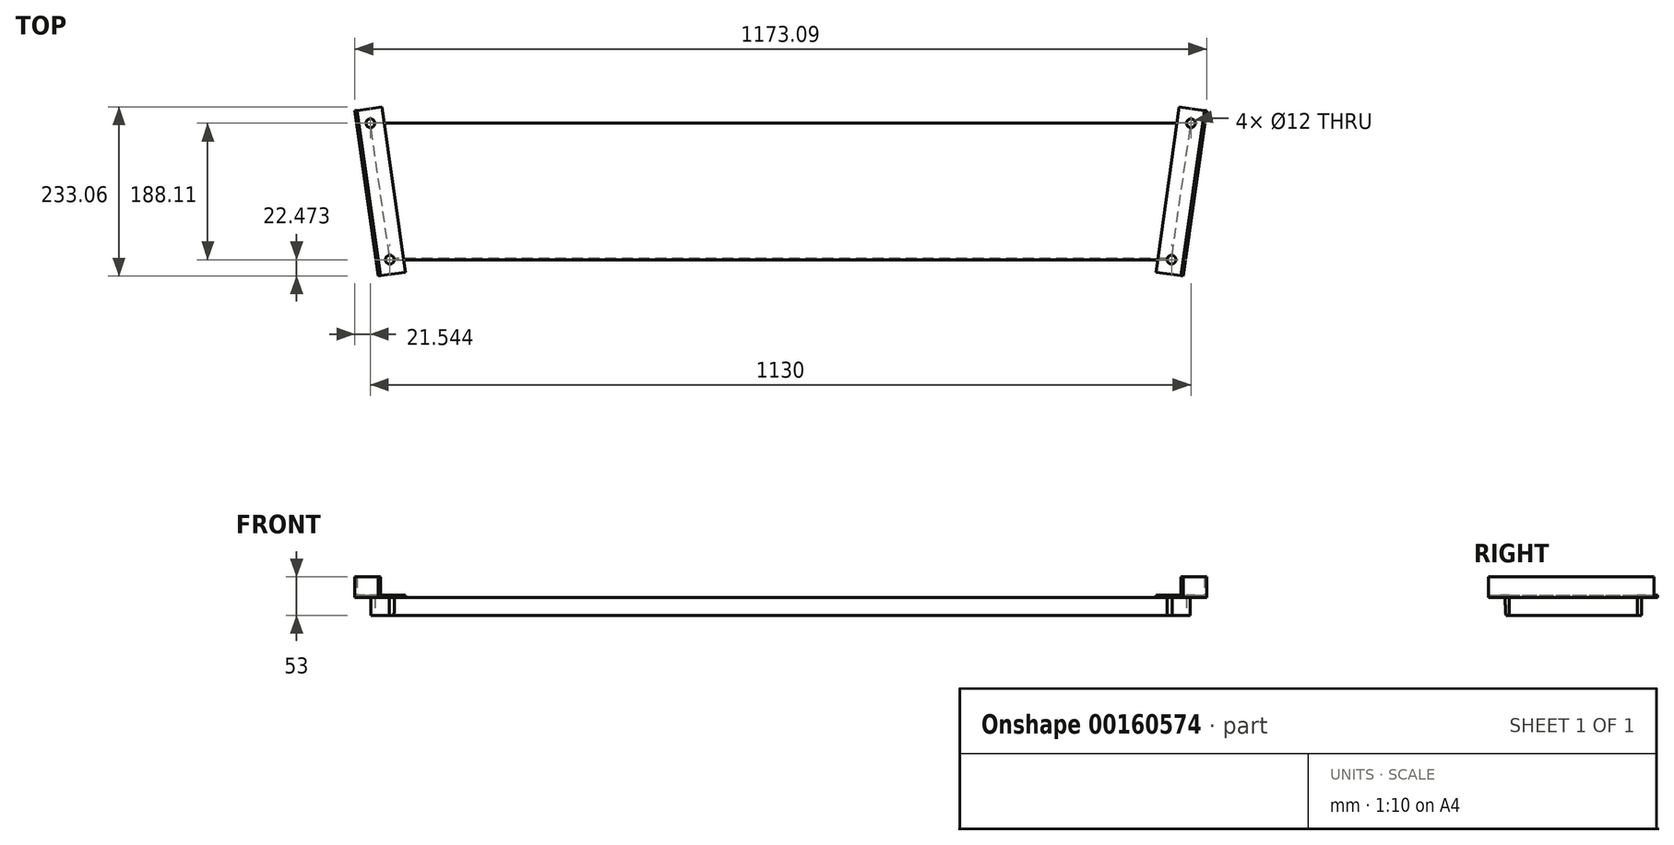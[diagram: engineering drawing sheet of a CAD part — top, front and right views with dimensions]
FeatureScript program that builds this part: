
annotation { "Feature Type Name" : "Feature", "Feature Type Description" : "" }
export const myFeature = defineFeature(function(context is Context, id is Id, definition is map)
    precondition{}
    {
        {
            var Q0;
            Q0=qCreatedBy(makeId("Top.planeOp"),FACE);
            var sketch = newSketch(context, id + "F0", { "sketchPlane" : qUnion([Q0])});
            skLineSegment(sketch, "E0.bottom", {"start": v(671.51, 132.18) * mm, "end": v(-458.49, 132.18) * mm});
            skCircle(sketch, "E1", {"center": v(671.51, 132.18) * mm, "radius": 6 * mm});
            skCircle(sketch, "E2", {"center": v(-458.49, 132.18) * mm, "radius": 6 * mm});
            skLineSegment(sketch, "E3", {"start": v(-431.75, -55.93) * mm, "end": v(-458.49, 132.18) * mm});
            skLineSegment(sketch, "E4", {"start": v(644.78, -55.93) * mm, "end": v(671.51, 132.18) * mm});
            skCircle(sketch, "E5", {"center": v(644.78, -55.93) * mm, "radius": 6 * mm});
            skLineSegment(sketch, "E6", {"start": v(-431.75, -55.93) * mm, "end": v(644.78, -55.93) * mm});
            skCircle(sketch, "E7", {"center": v(-431.75, -55.93) * mm, "radius": 6 * mm});
            skLineSegment(sketch, "E8", {"start": v(106.51, 132.18) * mm, "end": v(106.51, -55.93) * mm, "construction": true});
            skSolve(sketch);
        }
        {
            var Q0;
            {var subQ5=sQuery(id+"F0.wireOp",EDGE,"E0.bottom");var subQ7=sQuery(id+"F0.wireOp",EDGE,"E1");var subQ8=makeQuery(id+"F0.imprint","INTERSECT",VERTEX,{"derivedFrom":[subQ5,subQ7]});Q0=makeQuery(id+"F0.imprint","IMPRINT",FACE,{"disambiguationData":[TD([[makeQuery(id+"F0.imprint","IMPRINT",EDGE,{"disambiguationData":[TD([[subQ8,-1.0]])],"derivedFrom":subQ5}),1.0]])]});}
            extrude(context, id + "F1", {"entities" : qUnion([Q0]), "depth" : 25 * mm});
        }
        {
            var Q0;
            {var subQ0=sQuery(id+"F0.wireOp",EDGE,"E4");var subQ1=sQuery(id+"F0.wireOp",EDGE,"E0.bottom");var subQ2=makeQuery(id+"F0.imprint","INTERSECT",VERTEX,{"derivedFrom":[subQ1,subQ0]});Q0=makeQuery(id+"F0.imprint","IMPRINT",FACE,{"disambiguationData":[TD([[makeQuery(id+"F0.imprint","IMPRINT",EDGE,{"disambiguationData":[TD([[subQ2,-1.0]])],"derivedFrom":subQ1}),-1.0]])]});}
            var Q1;
            {var subQ0=sQuery(id+"F0.wireOp",EDGE,"E4");var subQ1=sQuery(id+"F0.wireOp",EDGE,"E0.bottom");var subQ2=makeQuery(id+"F0.imprint","INTERSECT",VERTEX,{"derivedFrom":[subQ1,subQ0]});Q1=makeQuery(id+"F0.imprint","IMPRINT",FACE,{"disambiguationData":[TD([[makeQuery(id+"F0.imprint","IMPRINT",EDGE,{"disambiguationData":[TD([[subQ2,-1.0]])],"derivedFrom":subQ1}),1.0]])]});}
            var Q2;
            {var subQ0=sQuery(id+"F0.wireOp",EDGE,"E6");var subQ1=sQuery(id+"F0.wireOp",EDGE,"E4");var subQ2=makeQuery(id+"F0.imprint","INTERSECT",VERTEX,{"derivedFrom":[subQ1,subQ0]});Q2=makeQuery(id+"F0.imprint","IMPRINT",FACE,{"disambiguationData":[TD([[makeQuery(id+"F0.imprint","IMPRINT",EDGE,{"disambiguationData":[TD([[subQ2,-1.0]])],"derivedFrom":subQ1}),1.0]])]});}
            var Q3;
            {var subQ0=sQuery(id+"F0.wireOp",EDGE,"E6");var subQ1=sQuery(id+"F0.wireOp",EDGE,"E4");var subQ2=makeQuery(id+"F0.imprint","INTERSECT",VERTEX,{"derivedFrom":[subQ1,subQ0]});Q3=makeQuery(id+"F0.imprint","IMPRINT",FACE,{"disambiguationData":[TD([[makeQuery(id+"F0.imprint","IMPRINT",EDGE,{"disambiguationData":[TD([[subQ2,-1.0]])],"derivedFrom":subQ1}),-1.0]])]});}
            var Q4;
            {var subQ0=sQuery(id+"F0.wireOp",EDGE,"E6");var subQ1=sQuery(id+"F0.wireOp",EDGE,"E3");var subQ2=makeQuery(id+"F0.imprint","INTERSECT",VERTEX,{"derivedFrom":[subQ1,subQ0]});Q4=makeQuery(id+"F0.imprint","IMPRINT",FACE,{"disambiguationData":[TD([[makeQuery(id+"F0.imprint","IMPRINT",EDGE,{"disambiguationData":[TD([[subQ2,-1.0]])],"derivedFrom":subQ1}),1.0]])]});}
            var Q5;
            {var subQ0=sQuery(id+"F0.wireOp",EDGE,"E6");var subQ1=sQuery(id+"F0.wireOp",EDGE,"E3");var subQ2=makeQuery(id+"F0.imprint","INTERSECT",VERTEX,{"derivedFrom":[subQ1,subQ0]});Q5=makeQuery(id+"F0.imprint","IMPRINT",FACE,{"disambiguationData":[TD([[makeQuery(id+"F0.imprint","IMPRINT",EDGE,{"disambiguationData":[TD([[subQ2,-1.0]])],"derivedFrom":subQ1}),-1.0]])]});}
            var Q6;
            {var subQ0=sQuery(id+"F0.wireOp",EDGE,"E3");var subQ1=sQuery(id+"F0.wireOp",EDGE,"E0.bottom");var subQ2=makeQuery(id+"F0.imprint","INTERSECT",VERTEX,{"derivedFrom":[subQ1,subQ0]});Q6=makeQuery(id+"F0.imprint","IMPRINT",FACE,{"disambiguationData":[TD([[makeQuery(id+"F0.imprint","IMPRINT",EDGE,{"disambiguationData":[TD([[subQ2,1.0]])],"derivedFrom":subQ1}),1.0]])]});}
            var Q7;
            {var subQ0=sQuery(id+"F0.wireOp",EDGE,"E3");var subQ1=sQuery(id+"F0.wireOp",EDGE,"E0.bottom");var subQ2=makeQuery(id+"F0.imprint","INTERSECT",VERTEX,{"derivedFrom":[subQ1,subQ0]});Q7=makeQuery(id+"F0.imprint","IMPRINT",FACE,{"disambiguationData":[TD([[makeQuery(id+"F0.imprint","IMPRINT",EDGE,{"disambiguationData":[TD([[subQ2,1.0]])],"derivedFrom":subQ1}),-1.0]])]});}
            extrude(context, id + "F2", {"entities" : qUnion([Q0, Q1, Q2, Q3, Q4, Q5, Q6, Q7]), "operationType" : NewBodyOperationType.REMOVE, "endBound" : BoundingType.THROUGH_ALL, "depth" : 50 * mm});
        }
        {
            var Q0;
            Q0=makeQuery(id+"F1.opExtrude","CAP_EDGE",EDGE,{"disambiguationData":[OSD([sQuery(id+"F0.wireOp",EDGE,"E6")])],"isStart":true});
            chamfer(context, id + "F3", {"entities" : qUnion([Q0]), "chamferType" : ChamferType.OFFSET_ANGLE, "width" : 25 * mm, "oppositeDirection" : false, "angle" : 3 * degree, "tangentPropagation" : true});
        }
        {
            var Q0;
            Q0=makeQuery(id+"F1.opExtrude","CAP_FACE",FACE,{"disambiguationData":[OSD([sQuery(id+"F0.wireOp",EDGE,"E0.bottom"),sQuery(id+"F0.wireOp",EDGE,"E1"),sQuery(id+"F0.wireOp",EDGE,"E2"),sQuery(id+"F0.wireOp",EDGE,"E3"),sQuery(id+"F0.wireOp",EDGE,"E4"),sQuery(id+"F0.wireOp",EDGE,"E5"),sQuery(id+"F0.wireOp",EDGE,"E6"),sQuery(id+"F0.wireOp",EDGE,"E7")])],"isStart":false});
            var sketch = newSketch(context, id + "F4", { "sketchPlane" : qUnion([Q0])});
            skLineSegment(sketch, "E9", {"start": v(671.51, 132.18) * mm, "end": v(690.33, 129.5) * mm, "construction": true});
            skLineSegment(sketch, "E10", {"start": v(671.51, 132.18) * mm, "end": v(652.7, 134.86) * mm, "construction": true});
            skLineSegment(sketch, "E11", {"start": v(671.51, 132.18) * mm, "end": v(674.33, 151.98) * mm, "construction": true});
            skLineSegment(sketch, "E12", {"start": v(644.78, -55.93) * mm, "end": v(641.97, -75.73) * mm, "construction": true});
            skLineSegment(sketch, "E13", {"start": v(674.33, 151.98) * mm, "end": v(693.06, 149.32) * mm});
            skLineSegment(sketch, "E14", {"start": v(641.97, -75.73) * mm, "end": v(660.78, -78.4) * mm});
            skLineSegment(sketch, "E15", {"start": v(660.78, -78.4) * mm, "end": v(693.06, 149.32) * mm});
            skLineSegment(sketch, "E16", {"start": v(674.33, 151.98) * mm, "end": v(655.52, 154.66) * mm});
            skLineSegment(sketch, "E17", {"start": v(641.97, -75.73) * mm, "end": v(623.16, -73.05) * mm});
            skLineSegment(sketch, "E18", {"start": v(623.16, -73.05) * mm, "end": v(655.52, 154.66) * mm});
            skCircle(sketch, "E19.0", {"center": v(671.51, 132.18) * mm, "radius": 6 * mm});
            skCircle(sketch, "E19.1", {"center": v(644.78, -55.93) * mm, "radius": 6 * mm});
            skSolve(sketch);
        }
        {
            var Q0;
            Q0=makeQuery(id+"F4.imprint","IMPRINT",FACE,{"disambiguationData":[TD([[makeQuery(id+"F4.imprint","IMPRINT",EDGE,{"derivedFrom":sQuery(id+"F4.wireOp",EDGE,"E13")}),-1.0]])]});
            var Q1;
            {var subQ0=sQuery(id+"F0.wireOp",EDGE,"E4");var subQ1=makeQuery(id+"F1.opExtrude","CAP_EDGE",EDGE,{"disambiguationData":[OSD([subQ0])],"isStart":false});Q1=makeQuery(id+"F4.imprint","IMPRINT",FACE,{"disambiguationData":[TD([[makeQuery(id+"F4.imprint","IMPRINT",EDGE,{"derivedFrom":subQ1}),1.0]])]});}
            extrude(context, id + "F5", {"entities" : qUnion([Q0, Q1]), "depth" : 3 * mm});
        }
        {
            var Q0;
            Q0=makeQuery(id+"F5.opExtrude","CAP_FACE",FACE,{"disambiguationData":[OSD([sQuery(id+"F4.wireOp",EDGE,"E13"),sQuery(id+"F4.wireOp",EDGE,"E14"),sQuery(id+"F4.wireOp",EDGE,"E15"),sQuery(id+"F4.wireOp",EDGE,"E16"),sQuery(id+"F4.wireOp",EDGE,"E17"),sQuery(id+"F4.wireOp",EDGE,"E18"),sQuery(id+"F4.wireOp",EDGE,"E19.0"),sQuery(id+"F4.wireOp",EDGE,"E19.1")])],"isStart":false});
            var sketch = newSketch(context, id + "F6", { "sketchPlane" : qUnion([Q0])});
            skLineSegment(sketch, "E20", {"start": v(660.78, -78.4) * mm, "end": v(657.8, -77.98) * mm});
            skLineSegment(sketch, "E21", {"start": v(657.8, -77.98) * mm, "end": v(690.17, 149.73) * mm});
            skSolve(sketch);
        }
        {
            var Q0;
            Q0=makeQuery(id+"F6.imprint","IMPRINT",FACE,{"disambiguationData":[TD([[makeQuery(id+"F6.imprint","IMPRINT",EDGE,{"derivedFrom":sQuery(id+"F6.wireOp",EDGE,"E20")}),-1.0]])]});
            extrude(context, id + "F7", {"entities" : qUnion([Q0]), "operationType" : NewBodyOperationType.ADD, "depth" : 25 * mm});
        }
        {
            var Q0;
            Q0=makeQuery(id+"F1.opExtrude","CAP_FACE",FACE,{"disambiguationData":[OSD([sQuery(id+"F0.wireOp",EDGE,"E0.bottom"),sQuery(id+"F0.wireOp",EDGE,"E1"),sQuery(id+"F0.wireOp",EDGE,"E2"),sQuery(id+"F0.wireOp",EDGE,"E3"),sQuery(id+"F0.wireOp",EDGE,"E4"),sQuery(id+"F0.wireOp",EDGE,"E5"),sQuery(id+"F0.wireOp",EDGE,"E6"),sQuery(id+"F0.wireOp",EDGE,"E7")])],"isStart":false});
            var sketch = newSketch(context, id + "F8", { "sketchPlane" : qUnion([Q0])});
            skLineSegment(sketch, "E22", {"start": v(106.51, 132.18) * mm, "end": v(106.51, -55.93) * mm});
            skLineSegment(sketch, "E23", {"start": v(106.51, 132.18) * mm, "end": v(106.51, -167.67) * mm, "construction": true});
            skSolve(sketch);
        }
        {
            var Q0;
            Q0=sQuery(id+"F0.wireOp",EDGE,"E8");
            var Q1;
            Q1=sQuery(id+"F8.wireOp",EDGE,"E23");
            cPlane(context, id + "F9", {"entities" : qUnion([Q0, Q1]), "cplaneType" : CPlaneType.LINE_ANGLE, "offset" : 25 * mm, "angle" : 0 * degree, "width" : 150 * mm, "height" : 150 * mm});
        }
        {
            var Q0;
            Q0=makeQuery(id+"F5.opExtrude","SWEPT_BODY",BODY,{"disambiguationData":[OSD([sQuery(id+"F4.wireOp",EDGE,"E13"),sQuery(id+"F4.wireOp",EDGE,"E14"),sQuery(id+"F4.wireOp",EDGE,"E15"),sQuery(id+"F4.wireOp",EDGE,"E16"),sQuery(id+"F4.wireOp",EDGE,"E17"),sQuery(id+"F4.wireOp",EDGE,"E18"),sQuery(id+"F4.wireOp",EDGE,"E19.0"),sQuery(id+"F4.wireOp",EDGE,"E19.1")])]});
            var Q1;
            Q1=qCreatedBy(id+"F9.planeOp",FACE);
            mirror(context, id + "F10", {"entities" : qUnion([Q0]), "mirrorPlane" : qUnion([Q1])});
        }
    });
